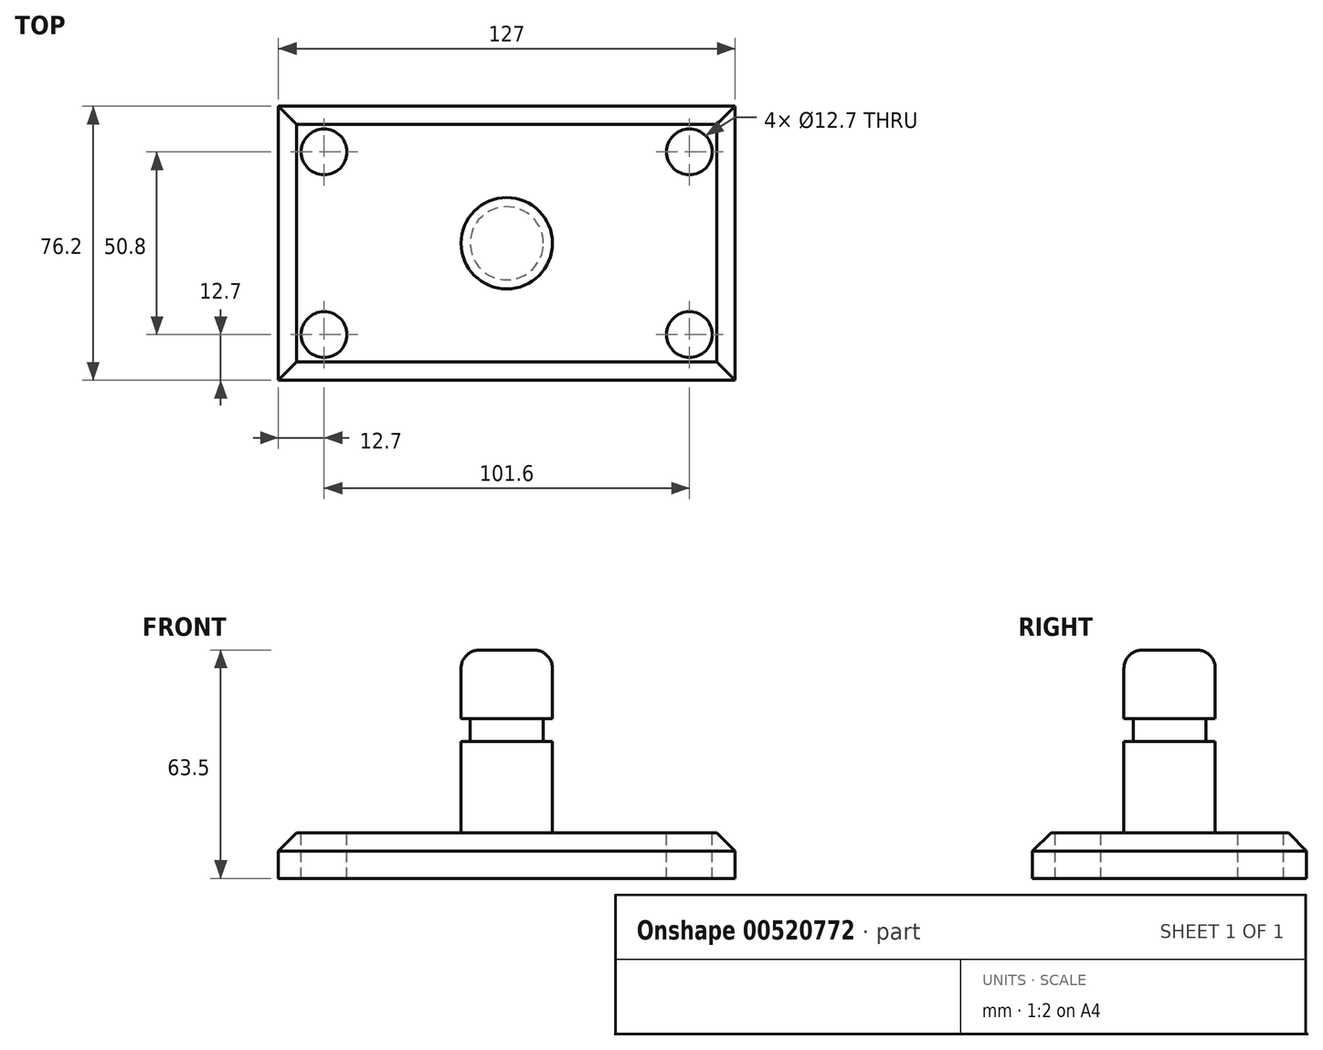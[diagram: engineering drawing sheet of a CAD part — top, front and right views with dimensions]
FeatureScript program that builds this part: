
annotation { "Feature Type Name" : "Feature", "Feature Type Description" : "" }
export const myFeature = defineFeature(function(context is Context, id is Id, definition is map)
    precondition{}
    {
        {
            var Q0;
            Q0=qCreatedBy(makeId("Top.planeOp"),FACE);
            var sketch = newSketch(context, id + "F0", { "sketchPlane" : qUnion([Q0])});
            skLineSegment(sketch, "E0.bottom", {"start": v(63.5, 38.1) * mm, "end": v(-63.5, 38.1) * mm});
            skLineSegment(sketch, "E0.top", {"start": v(63.5, -38.1) * mm, "end": v(-63.5, -38.1) * mm});
            skLineSegment(sketch, "E0.left", {"start": v(63.5, 38.1) * mm, "end": v(63.5, -38.1) * mm});
            skLineSegment(sketch, "E0.right", {"start": v(-63.5, 38.1) * mm, "end": v(-63.5, -38.1) * mm});
            skPoint(sketch, "E0.middle", {"position": v(0, 0) * mm});
            skSolve(sketch);
        }
        {
            var Q0;
            Q0=makeQuery(id+"F0.imprint","IMPRINT",FACE,{"disambiguationData":[TD([[makeQuery(id+"F0.imprint","IMPRINT",EDGE,{"derivedFrom":sQuery(id+"F0.wireOp",EDGE,"E0.bottom")}),1.0]])]});
            extrude(context, id + "F1", {"entities" : qUnion([Q0]), "depth" : 12.7 * mm, "offsetDistance" : 25.4 * mm});
        }
        {
            var Q0;
            Q0=makeQuery(id+"F1.opExtrude","CAP_FACE",FACE,{"disambiguationData":[OSD([sQuery(id+"F0.wireOp",EDGE,"E0.bottom"),sQuery(id+"F0.wireOp",EDGE,"E0.top"),sQuery(id+"F0.wireOp",EDGE,"E0.left"),sQuery(id+"F0.wireOp",EDGE,"E0.right")])],"isStart":false});
            var sketch = newSketch(context, id + "F2", { "sketchPlane" : qUnion([Q0])});
            skCircle(sketch, "E1", {"center": v(-50.8, -25.4) * mm, "radius": 6.35 * mm});
            skCircle(sketch, "E2", {"center": v(-50.8, 25.4) * mm, "radius": 6.35 * mm});
            skCircle(sketch, "E3", {"center": v(50.8, -25.4) * mm, "radius": 6.35 * mm});
            skCircle(sketch, "E4", {"center": v(50.8, 25.4) * mm, "radius": 6.35 * mm});
            skSolve(sketch);
        }
        {
            var Q0;
            Q0 = qSketchRegion(id + "F2", true);
            extrude(context, id + "F3", {"entities" : qUnion([Q0]), "operationType" : NewBodyOperationType.REMOVE, "endBound" : BoundingType.THROUGH_ALL, "oppositeDirection" : true, "depth" : 12.7 * mm, "offsetDistance" : 25.4 * mm});
        }
        {
            var Q0;
            Q0=qCreatedBy(makeId("Front.planeOp"),FACE);
            var sketch = newSketch(context, id + "F4", { "sketchPlane" : qUnion([Q0])});
            skLineSegment(sketch, "E5.bottom", {"start": v(0, 63.5) * mm, "end": v(12.7, 63.5) * mm});
            skLineSegment(sketch, "E5.top", {"start": v(0, 12.7) * mm, "end": v(12.7, 12.7) * mm});
            skLineSegment(sketch, "E5.left", {"start": v(0, 63.5) * mm, "end": v(0, 12.7) * mm});
            skLineSegment(sketch, "E5.right", {"start": v(12.7, 63.5) * mm, "end": v(12.7, 12.7) * mm});
            skSolve(sketch);
        }
        {
            var Q0;
            Q0 = qSketchRegion(id + "F4", true);
            var Q1;
            Q1=sQuery(id+"F4.wireOp",EDGE,"E5.left");
            revolve(context, id + "F5", {"operationType" : NewBodyOperationType.ADD, "entities" : qUnion([Q0]), "axis" : qUnion([Q1]), "revolveType" : RevolveType.FULL});
        }
        {
            var Q0;
            Q0=qCreatedBy(makeId("Front.planeOp"),FACE);
            var sketch = newSketch(context, id + "F6", { "sketchPlane" : qUnion([Q0])});
            skLineSegment(sketch, "E6.bottom", {"start": v(10.16, 44.45) * mm, "end": v(29.77, 44.45) * mm});
            skLineSegment(sketch, "E6.top", {"start": v(10.16, 38.1) * mm, "end": v(29.77, 38.1) * mm});
            skLineSegment(sketch, "E6.left", {"start": v(10.16, 44.45) * mm, "end": v(10.16, 38.1) * mm});
            skLineSegment(sketch, "E6.right", {"start": v(29.77, 44.45) * mm, "end": v(29.77, 38.1) * mm});
            skSolve(sketch);
        }
        {
            var Q0;
            Q0=makeQuery(id+"F6.imprint","IMPRINT",FACE,{"disambiguationData":[TD([[makeQuery(id+"F6.imprint","IMPRINT",EDGE,{"derivedFrom":sQuery(id+"F6.wireOp",EDGE,"E6.bottom")}),-1.0]])]});
            var Q1;
            Q1=sQuery(id+"F4.wireOp",EDGE,"E5.left");
            revolve(context, id + "F7", {"operationType" : NewBodyOperationType.REMOVE, "entities" : qUnion([Q0]), "axis" : qUnion([Q1]), "revolveType" : RevolveType.FULL});
        }
        {
            var Q0;
            Q0=makeQuery(id+"F5.opRevolve","SWEPT_EDGE",EDGE,{"disambiguationData":[OSD([sQuery(id+"F4.wireOp",EDGE,"E5.bottom"),sQuery(id+"F4.wireOp",EDGE,"E5.right")])]});
            var Q1;
            Q1=makeQuery(id+"F5.opRevolve","SWEPT_EDGE",EDGE,{"disambiguationData":[OSD([sQuery(id+"F4.wireOp",EDGE,"E5.top"),sQuery(id+"F4.wireOp",EDGE,"E5.right")])]});
            fillet(context, id + "F8", {"entities" : qUnion([Q0, Q1]), "radius" : 5.08 * mm, "tangentPropagation" : true, "allowEdgeOverflow" : false});
        }
        {
            var Q0;
            Q0=makeQuery(id+"F1.opExtrude","CAP_EDGE",EDGE,{"disambiguationData":[OSD([sQuery(id+"F0.wireOp",EDGE,"E0.right")])],"isStart":false});
            var Q1;
            Q1=makeQuery(id+"F1.opExtrude","CAP_EDGE",EDGE,{"disambiguationData":[OSD([sQuery(id+"F0.wireOp",EDGE,"E0.bottom")])],"isStart":false});
            var Q2;
            Q2=makeQuery(id+"F1.opExtrude","CAP_EDGE",EDGE,{"disambiguationData":[OSD([sQuery(id+"F0.wireOp",EDGE,"E0.top")])],"isStart":false});
            var Q3;
            Q3=makeQuery(id+"F1.opExtrude","CAP_EDGE",EDGE,{"disambiguationData":[OSD([sQuery(id+"F0.wireOp",EDGE,"E0.left")])],"isStart":false});
            chamfer(context, id + "F9", {"entities" : qUnion([Q0, Q1, Q2, Q3]), "width" : 5.08 * mm, "tangentPropagation" : true});
        }
    });
